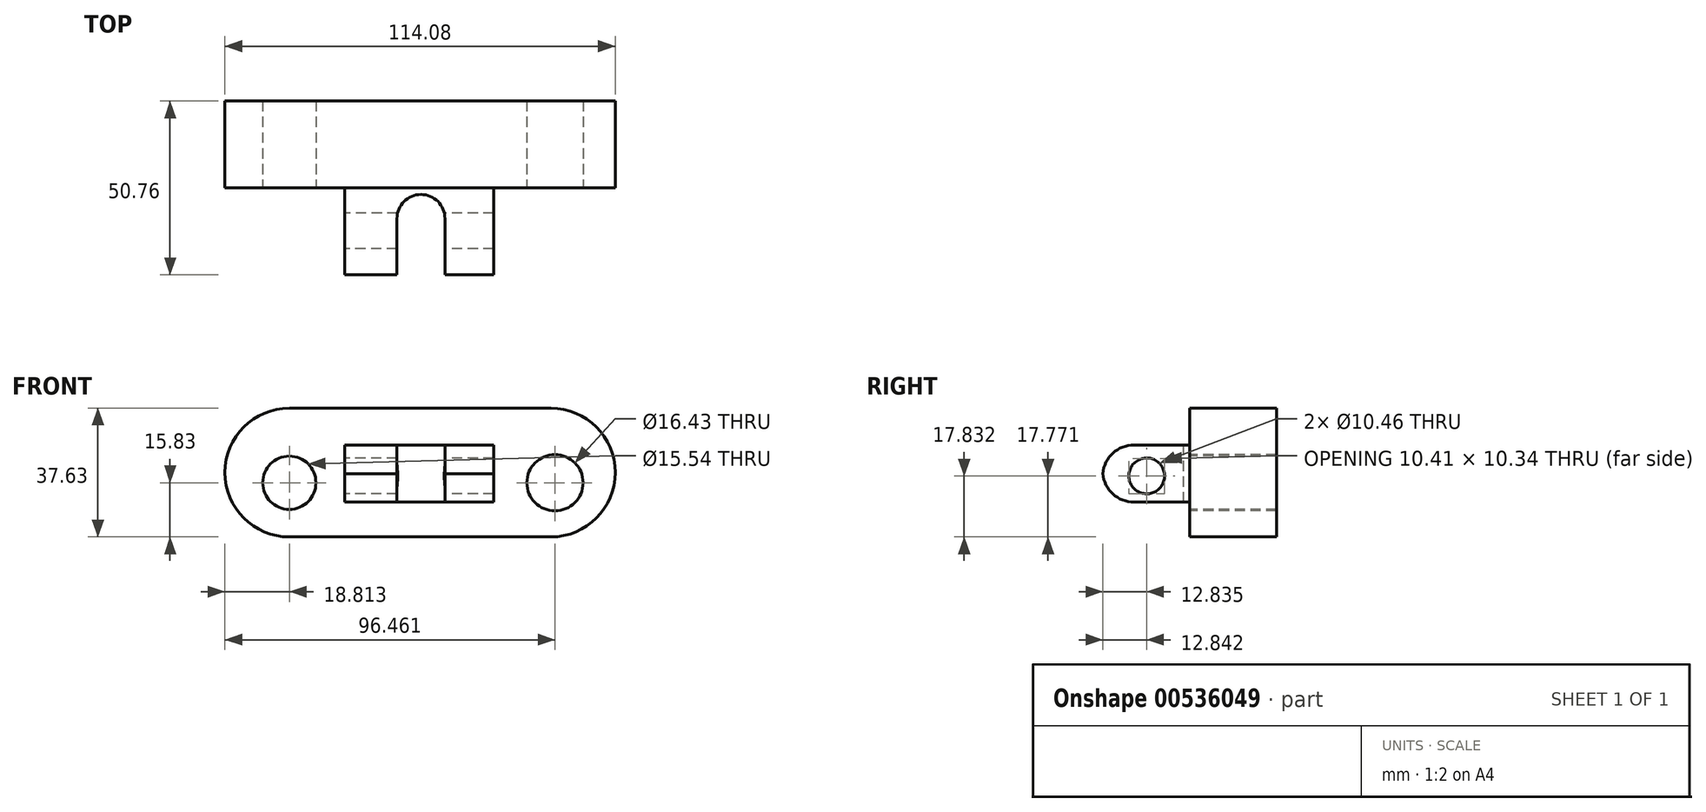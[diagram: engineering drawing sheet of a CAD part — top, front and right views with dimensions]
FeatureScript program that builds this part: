
annotation { "Feature Type Name" : "Feature", "Feature Type Description" : "" }
export const myFeature = defineFeature(function(context is Context, id is Id, definition is map)
    precondition{}
    {
        {
            var Q0;
            Q0=qCreatedBy(makeId("Front.planeOp"),FACE);
            var sketch = newSketch(context, id + "F0", { "sketchPlane" : qUnion([Q0])});
            skLineSegment(sketch, "E0.bottom", {"start": v(-22.7, 21.8) * mm, "end": v(53.76, 21.8) * mm});
            skLineSegment(sketch, "E0.top", {"start": v(-22.7, -15.83) * mm, "end": v(53.76, -15.83) * mm});
            skArc(sketch, "E1", {"start": v(53.76, -15.83) * mm, "mid": v(72.57, 2.99) * mm, "end": v(53.76, 21.8) * mm});
            skArc(sketch, "E2", {"start": v(-22.7, 21.8) * mm, "mid": v(-41.51, 2.99) * mm, "end": v(-22.7, -15.83) * mm});
            skSolve(sketch);
        }
        {
            var Q0;
            Q0 = qSketchRegion(id + "F0", true);
            extrude(context, id + "F1", {"entities" : qUnion([Q0]), "oppositeDirection" : true, "depth" : 25.4 * mm, "offsetDistance" : 25.4 * mm});
        }
        {
            var Q0;
            Q0=qCreatedBy(makeId("Front.planeOp"),FACE);
            var sketch = newSketch(context, id + "F2", { "sketchPlane" : qUnion([Q0])});
            skCircle(sketch, "E3", {"center": v(-22.7, 0) * mm, "radius": 7.77 * mm});
            skCircle(sketch, "E4", {"center": v(54.95, 0) * mm, "radius": 8.22 * mm});
            skSolve(sketch);
        }
        {
            var Q0;
            Q0 = qSketchRegion(id + "F2", true);
            extrude(context, id + "F3", {"entities" : qUnion([Q0]), "operationType" : NewBodyOperationType.REMOVE, "oppositeDirection" : true, "depth" : 25.4 * mm, "offsetDistance" : 25.4 * mm});
        }
        {
            var Q0;
            Q0=qCreatedBy(makeId("Front.planeOp"),FACE);
            var sketch = newSketch(context, id + "F4", { "sketchPlane" : qUnion([Q0])});
            skLineSegment(sketch, "E5.bottom", {"start": v(-6.57, 11.05) * mm, "end": v(37.03, 11.05) * mm});
            skLineSegment(sketch, "E5.top", {"start": v(-6.57, -5.67) * mm, "end": v(37.03, -5.67) * mm});
            skLineSegment(sketch, "E5.left", {"start": v(-6.57, 11.05) * mm, "end": v(-6.57, -5.67) * mm});
            skLineSegment(sketch, "E5.right", {"start": v(37.03, 11.05) * mm, "end": v(37.03, -5.67) * mm});
            skSolve(sketch);
        }
        {
            var Q0;
            Q0 = qSketchRegion(id + "F4", true);
            extrude(context, id + "F5", {"entities" : qUnion([Q0]), "operationType" : NewBodyOperationType.ADD, "depth" : 25.4 * mm, "offsetDistance" : 25.4 * mm});
        }
        {
            var Q0;
            Q0=qCreatedBy(makeId("Right.planeOp"),FACE);
            var sketch = newSketch(context, id + "F6", { "sketchPlane" : qUnion([Q0])});
            skCircle(sketch, "E6", {"center": v(-12.52, 2) * mm, "radius": 5.23 * mm});
            skPoint(sketch, "E6.first.point", {"position": v(-17.75, 2.03) * mm});
            skPoint(sketch, "E6.second.point", {"position": v(-7.7, 0) * mm});
            skPoint(sketch, "E6.third.point", {"position": v(-17.36, 0) * mm});
            skSolve(sketch);
        }
        {
            var Q0;
            Q0 = qSketchRegion(id + "F6", true);
            extrude(context, id + "F7", {"entities" : qUnion([Q0]), "operationType" : NewBodyOperationType.REMOVE, "depth" : 66.55 * mm, "offsetDistance" : 25.4 * mm});
        }
        {
            var Q0;
            Q0 = qSketchRegion(id + "F6", true);
            extrude(context, id + "F8", {"entities" : qUnion([Q0]), "operationType" : NewBodyOperationType.REMOVE, "oppositeDirection" : true, "depth" : 50.55 * mm, "offsetDistance" : 25.4 * mm});
        }
        {
            var Q0;
            Q0=makeQuery(id+"F5.opExtrude","SWEPT_FACE",FACE,{"disambiguationData":[OSD([sQuery(id+"F4.wireOp",EDGE,"E5.top")])]});
            var sketch = newSketch(context, id + "F9", { "sketchPlane" : qUnion([Q0])});
            skLineSegment(sketch, "E7.bottom", {"start": v(8.77, 25.4) * mm, "end": v(22.8, 25.4) * mm});
            skLineSegment(sketch, "E7.top", {"start": v(8.77, 8.93) * mm, "end": v(22.8, 8.93) * mm});
            skLineSegment(sketch, "E7.left", {"start": v(8.77, 25.4) * mm, "end": v(8.77, 8.93) * mm});
            skLineSegment(sketch, "E7.right", {"start": v(22.8, 25.4) * mm, "end": v(22.8, 8.93) * mm});
            skArc(sketch, "E8", {"start": v(8.77, 8.93) * mm, "mid": v(15.78, 1.91) * mm, "end": v(22.8, 8.93) * mm});
            skSolve(sketch);
        }
        {
            var Q0;
            Q0 = qSketchRegion(id + "F9", true);
            extrude(context, id + "F10", {"entities" : qUnion([Q0]), "operationType" : NewBodyOperationType.REMOVE, "endBound" : BoundingType.THROUGH_ALL, "oppositeDirection" : true, "depth" : 25.4 * mm, "offsetDistance" : 25.4 * mm});
        }
        {
            var Q0;
            {var subQ0=sQuery(id+"F4.wireOp",EDGE,"E5.left");var subQ1=sQuery(id+"F4.wireOp",EDGE,"E5.top");Q0=makeQuery(id+"F10.boolean.opBoolean","SPLIT",EDGE,{"disambiguationData":[TD([makeQuery(id+"F5.opExtrude","SWEPT_FACE",FACE,{"disambiguationData":[OSD([subQ0])]})])],"derivedFrom":makeQuery(id+"F5.opExtrude","CAP_EDGE",EDGE,{"disambiguationData":[OSD([subQ1])],"isStart":false})});}
            var Q1;
            {var subQ0=sQuery(id+"F4.wireOp",EDGE,"E5.bottom");var subQ1=sQuery(id+"F4.wireOp",EDGE,"E5.left");Q1=makeQuery(id+"F10.boolean.opBoolean","SPLIT",EDGE,{"disambiguationData":[TD([makeQuery(id+"F5.opExtrude","SWEPT_FACE",FACE,{"disambiguationData":[OSD([subQ1])]})])],"derivedFrom":makeQuery(id+"F5.opExtrude","CAP_EDGE",EDGE,{"disambiguationData":[OSD([subQ0])],"isStart":false})});}
            var Q2;
            {var subQ0=sQuery(id+"F4.wireOp",EDGE,"E5.right");var subQ1=sQuery(id+"F4.wireOp",EDGE,"E5.top");Q2=makeQuery(id+"F10.boolean.opBoolean","SPLIT",EDGE,{"disambiguationData":[TD([makeQuery(id+"F5.opExtrude","SWEPT_FACE",FACE,{"disambiguationData":[OSD([subQ0])]})])],"derivedFrom":makeQuery(id+"F5.opExtrude","CAP_EDGE",EDGE,{"disambiguationData":[OSD([subQ1])],"isStart":false})});}
            var Q3;
            {var subQ0=sQuery(id+"F4.wireOp",EDGE,"E5.bottom");var subQ1=sQuery(id+"F4.wireOp",EDGE,"E5.right");Q3=makeQuery(id+"F10.boolean.opBoolean","SPLIT",EDGE,{"disambiguationData":[TD([makeQuery(id+"F5.opExtrude","SWEPT_FACE",FACE,{"disambiguationData":[OSD([subQ1])]})])],"derivedFrom":makeQuery(id+"F5.opExtrude","CAP_EDGE",EDGE,{"disambiguationData":[OSD([subQ0])],"isStart":false})});}
            fillet(context, id + "F11", {"entities" : qUnion([Q0, Q1, Q2, Q3]), "radius" : 9.2 * mm, "tangentPropagation" : true, "allowEdgeOverflow" : false});
        }
    });
